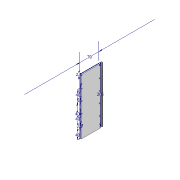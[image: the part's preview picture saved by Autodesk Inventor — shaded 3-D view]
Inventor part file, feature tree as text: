
AUTODESK INVENTOR PART (.ipt)
format: ipt  version: 2020.3 (Build 243373010, 373A)  size: 124,416 bytes
history: native  units: mm
features: sketch x3, extrude x3, hole x1
ambient origin geometry x8: Origin, YZ Plane, XZ Plane, XY Plane, X Axis, Y Axis, Z Axis, Center Point
bodies: Solid1 (feature_tree)
feature tree (7):
  sketch  "Sketch1"  dims[d0=205.0mm d1=70.0mm]
  extrude  "Extrusion1"  Depth=205.0mm
  hole  "Hole1"  [1 undecoded]
  extrude  "Extrusion2"  Depth=5.0mm TaperAngle=0.0deg
  extrude  "Extrusion3"  Depth=10.0mm TaperAngle=0.0deg
  sketch  "Sketch2"  dims[d2=2.0mm d3=2.0mm d4=2.0mm d5=2.0mm d7=40.0mm d8=40.0mm d9=40.0mm d10=2.5mm d11=40.0mm]
  sketch  "Sketch3"  dims[d12=2.5mm d13=5.0mm d14=0.0mm d15=3.242mm d16=8.0mm d17=4.0mm d18=2.0mm d19=90.0deg d20=11.8mm d21=0.0mm d22=10.0mm d23=0.0mm d24=10.0mm d25=2.5mm d26=4.0mm d27=3.0mm d28=10.0mm d29=0.0mm]
note: 1 required parameter value undecoded (feature->parameter linkage not recoverable at this tier; creation-order binding heuristic only, values carry confidence <= 0.55)
